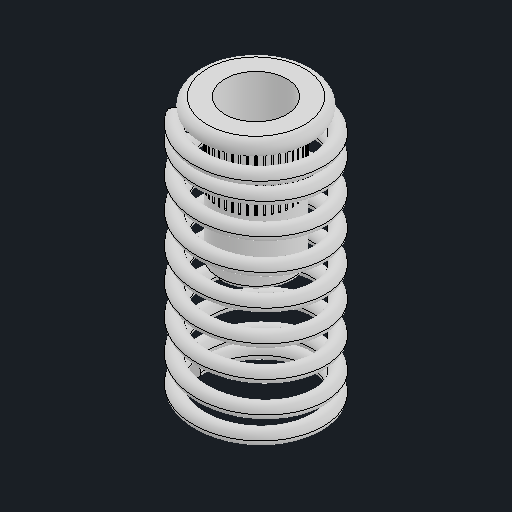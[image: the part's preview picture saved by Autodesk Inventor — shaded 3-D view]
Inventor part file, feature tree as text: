
AUTODESK INVENTOR PART (.ipt)
format: ipt  version: 2024.2 (Build 282272000, 272)  size: 1,220,096 bytes
history: native  units: mm
features: other x2, pattern_circular x1, sweep x1
ambient origin geometry x8: Origin, YZ Plane, XZ Plane, XY Plane, X Axis, Y Axis, Z Axis, Center Point
bodies: Body1 (feature_tree), Body2 (feature_tree)
feature tree (4):
  other  "솔리드1"
  other  "솔리드2"
  pattern_circular  "CirPattern2"
  sweep  "Sweep2"
